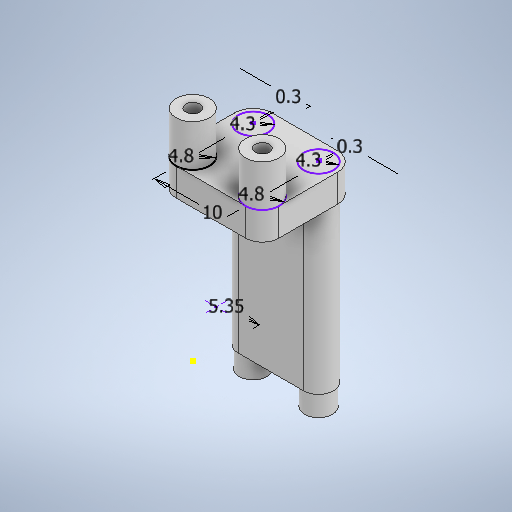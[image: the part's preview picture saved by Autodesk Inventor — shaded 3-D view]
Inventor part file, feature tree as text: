
AUTODESK INVENTOR PART (.ipt)
format: ipt  version: 2025.2 (Build 292293000, 293)  size: 540,672 bytes
history: native  units: in
note: dims shown in document units (in); Inventor stores cm internally (conversion verified against a paired STEP export)
features: sketch x10, extrude x10, projected_geometry x4
ambient origin geometry x8: Origin, YZ Plane, XZ Plane, XY Plane, X Axis, Y Axis, Z Axis, Center Point
bodies: Solid1 (feature_tree)
feature tree (24):
  sketch  "Sketch1"  dims[d0=0.189in d1=0.1693in]
  extrude  "Extrusion1"  Depth=0.1693in
  extrude  "Extrusion3"  Depth=0.3937in
  extrude  "Extrusion4"  Depth=0.2362in TaperAngle=0.0deg
  extrude  "Extrusion5"  Depth=0.3307in
  sketch  "Sketch6"  dims[d12=0.3307in d13=0.3307in]
  extrude  "Extrusion7"  Depth=0.1575in TaperAngle=0.0deg
  extrude  "Extrusion8"  Depth=0.2106in
  extrude  "Extrusion9"  Depth=0.1575in
  extrude  "Extrusion10"  Depth=0.1181in
  extrude  "Extrusion11"  Depth=0.2362in TaperAngle=0.0deg
  extrude  "Extrusion12"  Depth=0.4724in
  sketch  "Sketch3"  dims[d3=0.189in d4=0.3937in]
  sketch  "Sketch4"  dims[d5=0.1693in d6=0.2362in d7=0.0in]
  projected_geometry  "Projected Loop1"
  sketch  "Sketch7"  dims[d14=0.1575in d15=0.0in d16=1.0039in d17=0.0in]
  sketch  "Sketch8"  dims[d18=0.5965in d19=0.0in d24=0.2106in]
  sketch  "Sketch10"  dims[d25=0.1575in d26=0.1575in]
  projected_geometry  "Projected Loop2"
  sketch  "Sketch11"  dims[d27=0.0787in d28=0.0in d29=0.1181in]
  sketch  "Sketch12"  dims[d30=0.1181in d31=0.2362in d32=0.0in]
  projected_geometry  "Projected Loop3"
  sketch  "Sketch13"  dims[d33=0.0118in d34=0.0118in d35=0.3937in d36=0.0in d37=0.1575in d38=0.1575in d39=0.1181in d40=0.0in d41=0.0787in d42=0.0787in d43=0.4724in d44=0.0in d45=0.0787in d46=0.0787in d47=0.4724in d48=0.0in]
  projected_geometry  "Projected Loop4"
